# Revit family: Relation 30
name_source: partatom
category: Lighting Fixtures
revit_build: Autodesk Revit MEP 2012 (Build: 20110309_2315(x64)
units: mm (PartAtom-declared; Revit-internal decimal feet)

## types (6) — shared parameters
Assembly Code = D5020220
Ballast Number of Poles = 1
Body Material = Metal - Chrome
Bulb Material = Glass - White, High Luminance
Default Elevation = 1219 mm
Dimming Lamp Color Temperature Shift = <None>
Emit from Line Length = 1829 mm
Length = 1829 mm
Light Source Symbol Size = 610 mm
Load Classification = Lighting - Dwelling Unit
Shade Material = Glass - Frosted

## per-type parameters (varying)
| type | Apparent Load | Ballast Voltage | Color Filter | Lamp |
| 100W - 120V | 100 VA | 120 V | 16777215 | A-19 |
| 100W - 277V | 100 VA | 277 V | 16777215 | A-19 |
| 150W - 120V | 150 VA | 120 V | 16777215 | A-21 |
| 150W - 277V | 150 VA | 277 V | 16777215 | A-21 |
| 100W - 120V Red | 100 VA | 120 V | 255 | A-19 |
| 100W - 120V Blue | 100 VA | 120 V | 16060449 | A-19 |

## geometry (parser evidence)
native form markers: Sweep x2
no freeform markers — native parametric forms only
